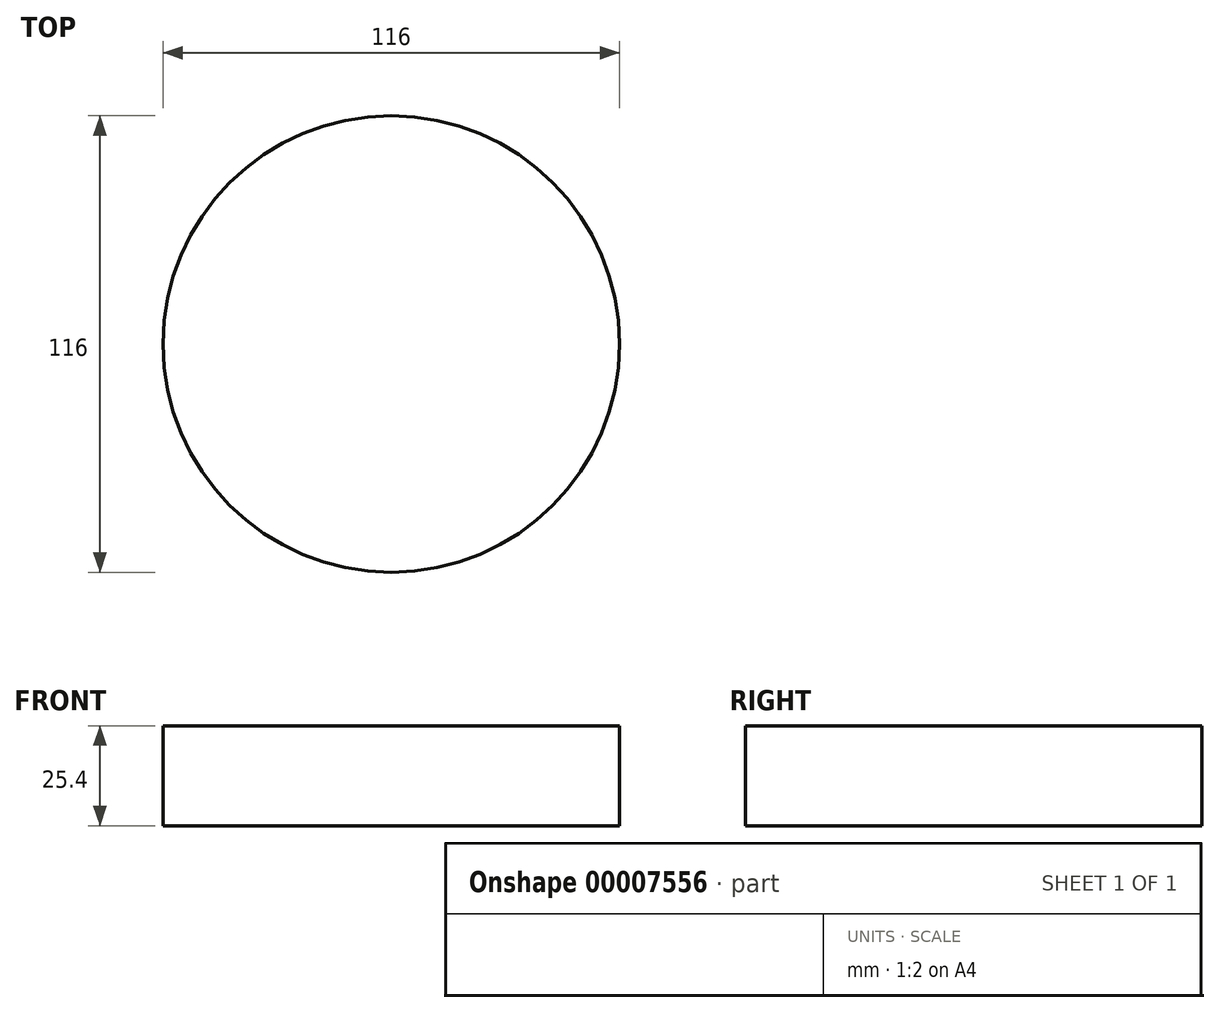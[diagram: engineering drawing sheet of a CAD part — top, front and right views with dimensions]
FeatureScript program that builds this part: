
annotation { "Feature Type Name" : "Feature", "Feature Type Description" : "" }
export const myFeature = defineFeature(function(context is Context, id is Id, definition is map)
    precondition{}
    {
        {
            var Q0;
            Q0=qCreatedBy(makeId("Top.planeOp"),FACE);
            var sketch = newSketch(context, id + "F0", { "sketchPlane" : qUnion([Q0])});
            skCircle(sketch, "E0", {"center": v(0, 0) * mm, "radius": 58 * mm});
            skSolve(sketch);
        }
        {
            var Q0;
            Q0=makeQuery(id+"F0.imprint","IMPRINT",FACE,{"disambiguationData":[TD([[makeQuery(id+"F0.imprint","IMPRINT",EDGE,{"derivedFrom":sQuery(id+"F0.wireOp",EDGE,"E0")}),1.0]])]});
            extrude(context, id + "F1", {"entities" : qUnion([Q0]), "depth" : 25.4 * mm});
        }
    });
